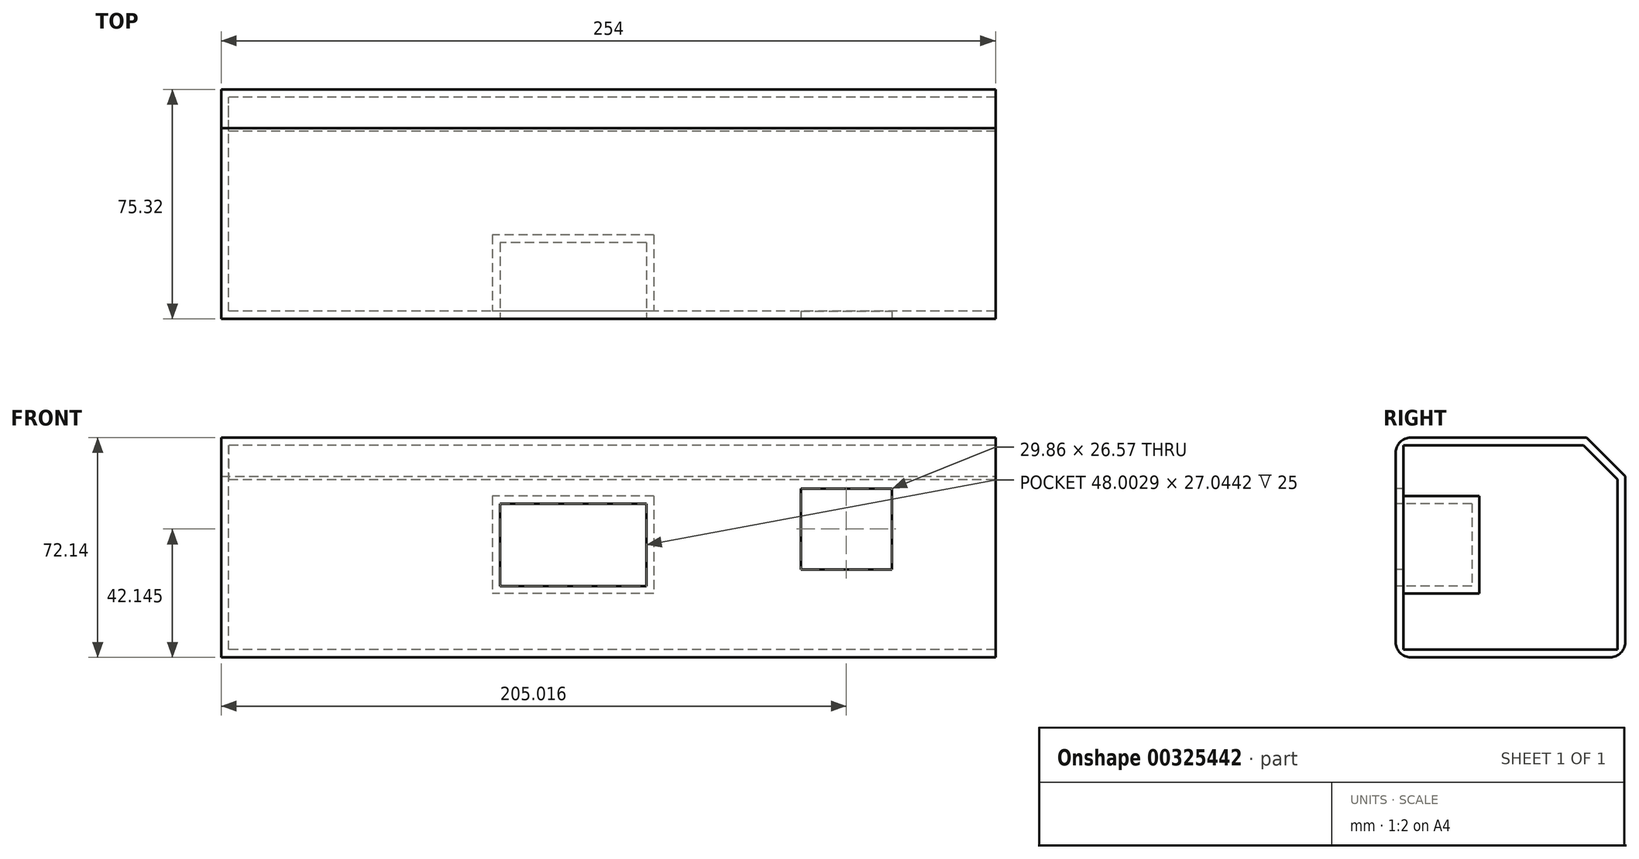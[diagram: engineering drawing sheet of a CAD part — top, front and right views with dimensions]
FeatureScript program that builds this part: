
annotation { "Feature Type Name" : "Feature", "Feature Type Description" : "" }
export const myFeature = defineFeature(function(context is Context, id is Id, definition is map)
    precondition{}
    {
        {
            var Q0;
            Q0=qCreatedBy(makeId("Right.planeOp"),FACE);
            var sketch = newSketch(context, id + "F0", { "sketchPlane" : qUnion([Q0])});
            skLineSegment(sketch, "E0.bottom", {"start": v(60.44, -13.53) * mm, "end": v(135.76, -13.53) * mm});
            skLineSegment(sketch, "E0.top", {"start": v(60.44, 58.6) * mm, "end": v(135.76, 58.6) * mm});
            skLineSegment(sketch, "E0.left", {"start": v(60.44, -13.53) * mm, "end": v(60.44, 58.6) * mm});
            skLineSegment(sketch, "E0.right", {"start": v(135.76, -13.53) * mm, "end": v(135.76, 58.6) * mm});
            skSolve(sketch);
        }
        {
            var Q0;
            Q0=makeQuery(id+"F0.imprint","IMPRINT",FACE,{"disambiguationData":[TD([[makeQuery(id+"F0.imprint","IMPRINT",EDGE,{"derivedFrom":sQuery(id+"F0.wireOp",EDGE,"E0.bottom")}),1.0]])]});
            extrude(context, id + "F1", {"entities" : qUnion([Q0]), "depth" : 254 * mm});
        }
        {
            var Q0;
            Q0=makeQuery(id+"F1.opExtrude","SWEPT_EDGE",EDGE,{"disambiguationData":[OSD([sQuery(id+"F0.wireOp",EDGE,"E0.top"),sQuery(id+"F0.wireOp",EDGE,"E0.right")])]});
            chamfer(context, id + "F2", {"entities" : qUnion([Q0]), "width" : 12.7 * mm, "tangentPropagation" : true});
        }
        {
            var Q0;
            Q0=makeQuery(id+"F1.opExtrude","SWEPT_FACE",FACE,{"disambiguationData":[OSD([sQuery(id+"F0.wireOp",EDGE,"E0.left")])]});
            var sketch = newSketch(context, id + "F3", { "sketchPlane" : qUnion([Q0])});
            skLineSegment(sketch, "E1.bottom", {"start": v(139.44, 36.93) * mm, "end": v(91.44, 36.93) * mm});
            skLineSegment(sketch, "E1.top", {"start": v(139.44, 9.88) * mm, "end": v(91.44, 9.88) * mm});
            skLineSegment(sketch, "E1.left", {"start": v(139.44, 36.93) * mm, "end": v(139.44, 9.88) * mm});
            skLineSegment(sketch, "E1.right", {"start": v(91.44, 36.93) * mm, "end": v(91.44, 9.88) * mm});
            skSolve(sketch);
        }
        {
            var Q0;
            Q0 = qSketchRegion(id + "F3", true);
            var Q1;
            Q1=makeQuery(id+"F3.imprint","IMPRINT",FACE,{"disambiguationData":[TD([[makeQuery(id+"F3.imprint","IMPRINT",EDGE,{"derivedFrom":sQuery(id+"F3.wireOp",EDGE,"E1.bottom")}),1.0]])]});
            extrude(context, id + "F4", {"entities" : qUnion([Q0, Q1]), "operationType" : NewBodyOperationType.REMOVE, "oppositeDirection" : true, "depth" : 25 * mm});
        }
        {
            var Q0;
            Q0=makeQuery(id+"F1.opExtrude","CAP_FACE",FACE,{"disambiguationData":[OSD([sQuery(id+"F0.wireOp",EDGE,"E0.bottom"),sQuery(id+"F0.wireOp",EDGE,"E0.top"),sQuery(id+"F0.wireOp",EDGE,"E0.left"),sQuery(id+"F0.wireOp",EDGE,"E0.right")])],"isStart":false});
            shell(context, id + "F5", {"entities" : qUnion([Q0]), "thickness" : 2.5 * mm});
        }
        {
            var Q0;
            Q0=makeQuery(id+"F1.opExtrude","SWEPT_EDGE",EDGE,{"disambiguationData":[OSD([sQuery(id+"F0.wireOp",EDGE,"E0.bottom"),sQuery(id+"F0.wireOp",EDGE,"E0.left")])]});
            var Q1;
            Q1=makeQuery(id+"F1.opExtrude","SWEPT_EDGE",EDGE,{"disambiguationData":[OSD([sQuery(id+"F0.wireOp",EDGE,"E0.top"),sQuery(id+"F0.wireOp",EDGE,"E0.left")])]});
            var Q2;
            Q2=makeQuery(id+"F1.opExtrude","SWEPT_EDGE",EDGE,{"disambiguationData":[OSD([sQuery(id+"F0.wireOp",EDGE,"E0.bottom"),sQuery(id+"F0.wireOp",EDGE,"E0.right")])]});
            fillet(context, id + "F6", {"entities" : qUnion([Q0, Q1, Q2]), "radius" : 5 * mm, "tangentPropagation" : true, "allowEdgeOverflow" : false});
        }
        {
            var Q0;
            Q0=makeQuery(id+"F1.opExtrude","SWEPT_FACE",FACE,{"disambiguationData":[OSD([sQuery(id+"F0.wireOp",EDGE,"E0.left")])]});
            var sketch = newSketch(context, id + "F7", { "sketchPlane" : qUnion([Q0])});
            skLineSegment(sketch, "E2.bottom", {"start": v(190.08, 41.9) * mm, "end": v(219.95, 41.9) * mm});
            skLineSegment(sketch, "E2.top", {"start": v(190.08, 15.33) * mm, "end": v(219.95, 15.33) * mm});
            skLineSegment(sketch, "E2.left", {"start": v(190.08, 41.9) * mm, "end": v(190.08, 15.33) * mm});
            skLineSegment(sketch, "E2.right", {"start": v(219.95, 41.9) * mm, "end": v(219.95, 15.33) * mm});
            skSolve(sketch);
        }
        {
            var Q0;
            Q0=makeQuery(id+"F7.imprint","IMPRINT",FACE,{"disambiguationData":[TD([[makeQuery(id+"F7.imprint","IMPRINT",EDGE,{"derivedFrom":sQuery(id+"F7.wireOp",EDGE,"E2.bottom")}),-1.0]])]});
            extrude(context, id + "F8", {"entities" : qUnion([Q0]), "operationType" : NewBodyOperationType.REMOVE, "oppositeDirection" : true, "depth" : 25 * mm});
        }
    });
